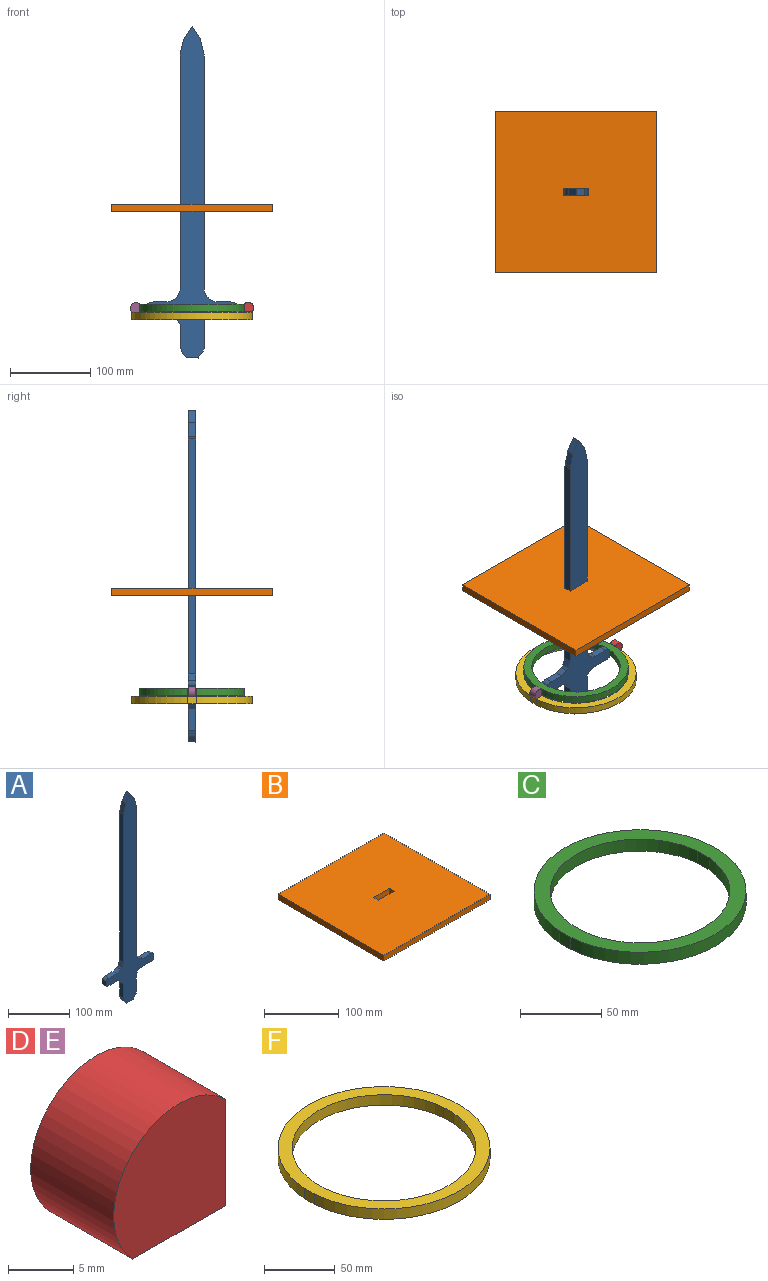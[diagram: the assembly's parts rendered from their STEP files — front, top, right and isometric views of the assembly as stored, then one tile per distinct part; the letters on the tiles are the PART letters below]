
ASSEMBLY  parts=6 mates=5
PART A: 39 faces, bbox 110x9x414.7 mm
  f0: plane 20.39x9mm, normal (0,0,-1), area 183.5mm2, adj f21,f22,f24,f29
  f1: plane 9x0.29mm, normal (-0.45,0,-0.89), area 2.9mm2, adj f21,f22,f28,f29
  f2: plane 27.91x9mm, normal (-1,0,0), area 251.2mm2, adj f21,f22,f27,f28
  f3: plane 9x6.61mm, normal (-0.8,0,-0.6), area 74.4mm2, adj f4,f21,f22,f27
  f4: plane 15x9mm, normal (0,0,-1), area 135mm2, adj f3,f5,f21,f22
  f5: plane 9x8.71mm, normal (0.8,0,-0.6), area 97.9mm2, adj f4,f21,f22,f31
  f6: plane 35.38x9mm, normal (1,0,0), area 318.4mm2, adj f21,f22,f31,f32
  f7: plane 9x6.29mm, normal (0.45,0,-0.89), area 63.3mm2, adj f21,f22,f30,f32
  f8: plane 22.24x9mm, normal (0,0,-1), area 200.2mm2, adj f21,f22,f25,f30
  f9: plane 10x9mm, normal (1,0,0), area 90mm2, adj f21,f22,f25,f26
  f10: plane 18.39x9mm, normal (0,0,1), area 165.5mm2, adj f21,f22,f26,f35
  f11: plane 9x2.93mm, normal (0.71,0,0.71), area 37.3mm2, adj f21,f22,f34,f35
  f12: plane 293.49x9mm, normal (1,0,0), area 2641.4mm2, adj f21,f22,f33,f34
  f13: plane 18.26x9mm, normal (0.97,0,0.25), area 169.5mm2, adj f14,f21,f22,f33
  f14: plane 15x10mm, normal (0.83,0,0.55), area 162.2mm2, adj f13,f15,f21,f22
  f15: plane 15x10mm, normal (-0.83,0,0.55), area 162.2mm2, adj f14,f16,f21,f22
  f16: plane 18.26x9mm, normal (-0.97,0,0.25), area 169.5mm2, adj f15,f21,f22,f36
  f17: plane 293.49x9mm, normal (-1,0,0), area 2641.4mm2, adj f21,f22,f36,f37
  f18: plane 9x2.93mm, normal (-0.71,0,0.71), area 37.3mm2, adj f21,f22,f37,f38
  f19: plane 18.39x9mm, normal (0,0,1), area 165.5mm2, adj f21,f22,f23,f38
  f20: plane 10x9mm, normal (-1,0,0), area 90mm2, adj f21,f22,f23,f24
  f21: plane 414.72x110mm, normal (0,-1,0), area 13359.7mm2, adj f0,f1,f2,f3,f4,f5,f6,f7
  f22: plane 414.72x110mm, normal (0,1,0), area 13359.7mm2, adj f0,f1,f2,f3,f4,f5,f6,f7
  f23: cylinder r=10mm len=9mm, axis (0,1,0), area 65mm2, adj f19,f20,f21,f22
  f24: cylinder r=10mm len=9mm, axis (0,1,0), area 65mm2, adj f0,f20,f21,f22
  f25: cylinder r=10mm len=9mm, axis (0,-1,0), area 65mm2, adj f8,f9,f21,f22
  f26: cylinder r=10mm len=9mm, axis (0,-1,0), area 65mm2, adj f9,f10,f21,f22
  f27: plane 9x7.63mm, normal (-0.95,0,-0.32), area 72.3mm2, adj f2,f3,f21,f22
  f28: plane 11.37x9mm, normal (-0.85,0,-0.53), area 120.3mm2, adj f1,f2,f21,f22
  f29: plane 9x5.68mm, normal (-0.23,0,-0.97), area 52.6mm2, adj f0,f1,f21,f22
  f30: plane 9x2.17mm, normal (0.23,0,-0.97), area 20.1mm2, adj f7,f8,f21,f22
  f31: plane 9x2.91mm, normal (0.95,0,-0.32), area 27.6mm2, adj f5,f6,f21,f22
  f32: plane 9x4.34mm, normal (0.85,0,-0.53), area 45.9mm2, adj f6,f7,f21,f22
  f33: plane 9x2.97mm, normal (0.99,0,0.12), area 26.9mm2, adj f12,f13,f21,f22
  f34: plane 9x8.54mm, normal (0.92,0,0.38), area 83.1mm2, adj f11,f12,f21,f22
  f35: plane 9x8.54mm, normal (0.38,0,0.92), area 83.1mm2, adj f10,f11,f21,f22
  f36: plane 9x2.97mm, normal (-0.99,0,0.12), area 26.9mm2, adj f16,f17,f21,f22
  f37: plane 9x8.54mm, normal (-0.92,0,0.38), area 83.1mm2, adj f17,f18,f21,f22
  f38: plane 9x8.54mm, normal (-0.38,0,0.92), area 83.1mm2, adj f18,f19,f21,f22
PART B: 10 faces, bbox 200x200x9 mm
  f0: plane 9x9mm, normal (1,0,0), area 81mm2, adj f1,f7,f8,f9
  f1: plane 30x9mm, normal (0,-1,0), area 270mm2, adj f0,f2,f8,f9
  f2: plane 9x9mm, normal (-1,0,0), area 81mm2, adj f1,f7,f8,f9
  f3: plane 200x9mm, normal (1,0,0), area 1800mm2, adj f4,f6,f8,f9
  f4: plane 200x9mm, normal (0,1,0), area 1800mm2, adj f3,f5,f8,f9
  f5: plane 200x9mm, normal (-1,0,0), area 1800mm2, adj f4,f6,f8,f9
  f6: plane 200x9mm, normal (0,-1,0), area 1800mm2, adj f3,f5,f8,f9
  f7: plane 30x9mm, normal (0,1,0), area 270mm2, adj f0,f2,f8,f9
  f8: plane 200x200mm, normal (0,0,1), area 39730mm2, adj f0,f1,f2,f3,f4,f5,f6,f7
  f9: plane 200x200mm, normal (0,0,-1), area 39730mm2, adj f0,f1,f2,f3,f4,f5,f6,f7
PART C: 10 faces, bbox 130x130.4x9 mm
  f0: plane 10x9mm, normal (1,0,0), area 90mm2, adj f1,f7,f8,f9
  f1: cylinder r=55.23mm len=110mm, axis (0,0,-1), area 1471.4mm2, adj f0,f2,f8,f9
  f2: plane 10x9mm, normal (-1,0,0), area 90mm2, adj f1,f7,f8,f9
  f3: cylinder r=65.19mm len=130mm, axis (0,0,-1), area 1753.2mm2, adj f4,f6,f8,f9
  f4: plane 10x9mm, normal (1,0,0), area 90mm2, adj f3,f5,f8,f9
  f5: cylinder r=65.19mm len=130mm, axis (0,0,-1), area 1753.2mm2, adj f4,f6,f8,f9
  f6: plane 10x9mm, normal (-1,0,0), area 90mm2, adj f3,f5,f8,f9
  f7: cylinder r=55.23mm len=110mm, axis (0,0,-1), area 1471.4mm2, adj f0,f2,f8,f9
  f8: plane 130.38x130mm, normal (0,0,1), area 3770.4mm2, adj f0,f1,f2,f3,f4,f5,f6,f7
  f9: plane 130.38x130mm, normal (0,0,-1), area 3770.4mm2, adj f0,f1,f2,f3,f4,f5,f6,f7
PART D: 5 faces, bbox 12.1x9x12.1 mm
  f0: plane 10x9mm, normal (1,0,0), area 90mm2, adj f1,f2,f3,f4
  f1: cylinder r=7.07mm len=12.07mm, axis (0,1,0), area 199.9mm2, adj f0,f2,f3,f4
  f2: plane 10x9mm, normal (0,0,-1), area 90mm2, adj f0,f1,f3,f4
  f3: plane 12.07x12.07mm, normal (0,-1,0), area 128.5mm2, adj f0,f1,f2
  f4: plane 12.07x12.07mm, normal (0,1,0), area 128.5mm2, adj f0,f1,f2
PART E: same geometry as D
PART F: 10 faces, bbox 150x150.3x9 mm
  f0: plane 10x9mm, normal (1,0,0), area 90mm2, adj f1,f7,f8,f9
  f1: cylinder r=75.17mm len=150mm, axis (0,0,-1), area 2035.2mm2, adj f0,f2,f8,f9
  f2: plane 10x9mm, normal (-1,0,0), area 90mm2, adj f1,f7,f8,f9
  f3: cylinder r=65.19mm len=130mm, axis (0,0,-1), area 1753.2mm2, adj f4,f6,f8,f9
  f4: plane 10x9mm, normal (-1,0,0), area 90mm2, adj f3,f5,f8,f9
  f5: cylinder r=65.19mm len=130mm, axis (0,0,-1), area 1753.2mm2, adj f4,f6,f8,f9
  f6: plane 10x9mm, normal (1,0,0), area 90mm2, adj f3,f5,f8,f9
  f7: cylinder r=75.17mm len=150mm, axis (0,0,-1), area 2035.2mm2, adj f0,f2,f8,f9
  f8: plane 150.33x150mm, normal (0,0,1), area 4398.6mm2, adj f0,f1,f2,f3,f4,f5,f6,f7
  f9: plane 150.33x150mm, normal (0,0,-1), area 4398.6mm2, adj f0,f1,f2,f3,f4,f5,f6,f7
PLACE A t=(13.75,163.02,72.05)mm
PLACE B t=(13.72,158.52,-63.2)mm
PLACE C t=(13.75,158.52,-188.29)mm
PLACE D rot(axis=(0,0,1),180deg) t=(88.75,154.02,-188.79)mm
PLACE E rot(axis=(-0.71,0,0.71),180deg) t=(-51.25,154.02,-179.29)mm
PLACE F t=(13.75,158.52,-198.29)mm
MATE fastened C.f2 <-> A.f9  axis (-1,0,0) through (68.75,158.52,-183.79)mm
MATE fastened A.f22 <-> B.f1  axis (0,1,0) through (13.72,163.02,-58.7)mm
MATE fastened D.f0 <-> C.f4  axis (-1,0,0) through (78.75,158.52,-183.79)mm
MATE fastened E.f2 <-> C.f6  axis (1,0,0) through (-51.25,158.52,-179.29)mm
MATE fastened F.f8 <-> E.f0  axis (0,0,1) through (-61.25,158.52,-189.29)mm
